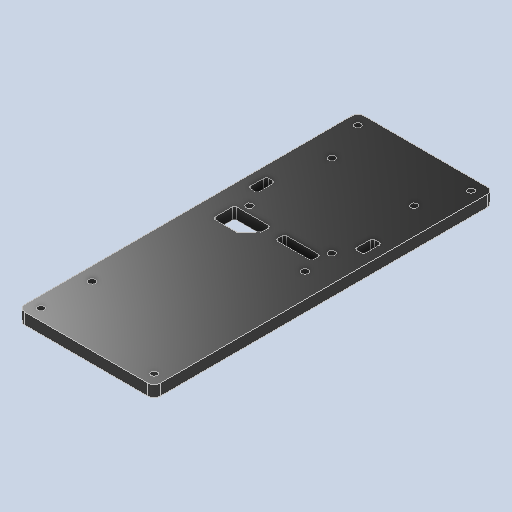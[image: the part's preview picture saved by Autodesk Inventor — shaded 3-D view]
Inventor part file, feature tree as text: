
AUTODESK INVENTOR PART (.ipt)
format: ipt  version: 2023 (Build 270158000, 158)  size: 358,912 bytes
history: native  units: in
note: dims shown in document units (in); Inventor stores cm internally (conversion verified against a paired STEP export)
features: extrude x6, fillet x3, sketch x1
ambient origin geometry x8: Origin, YZ Plane, XZ Plane, XY Plane, X Axis, Y Axis, Z Axis, Center Point
bodies: Solid1 (feature_tree)
feature tree (10):
  sketch  "Sketch1"  dims[d10=2.3622in d11=5.9055in d12=0.1969in d13=0.1969in d14=0.1969in d15=0.1969in d16=0.1969in d17=0.1969in d18=0.1969in d19=0.1969in d20=0.1102in d21=0.1102in d22=0.1102in d23=0.1102in d24=0.1969in d25=0.0in d26=0.1102in d27=0.1102in d28=0.7874in d29=0.8465in d30=1.6929in d31=0.8465in d32=1.4331in d33=1.4331in d34=0.1181in d35=0.1181in d36=0.1181in d37=0.1181in d38=0.426in d39=3.0472in d40=0.2362in d41=1.0472in d42=0.1181in d43=0.1181in d44=0.3937in d45=0.0in d46=0.3937in d47=0.0in d48=0.3937in d49=0.1575in d50=0.315in d51=0.1575in d52=0.315in d53=0.2362in d54=0.3937in d55=0.1575in d56=0.1969in d57=0.6299in d58=0.1575in d59=0.3937in d60=0.0in d61=0.3937in d62=0.0in d63=0.3937in d64=0.0in d65=0.0394in]
  extrude  "Extrusion1"  Depth=5.9055in
  fillet  "Fillet1"  Radius=0.1969in
  fillet  "Fillet2"  Radius=0.1969in
  extrude  "Extrusion2"  Depth=0.1969in
  extrude  "Extrusion3"  Depth=0.1969in
  extrude  "Extrusion4"  Depth=0.1969in
  extrude  "Extrusion5"  Depth=0.1969in
  extrude  "Extrusion6"  Depth=0.1969in
  fillet  "Fillet3"  Radius=0.1969in
